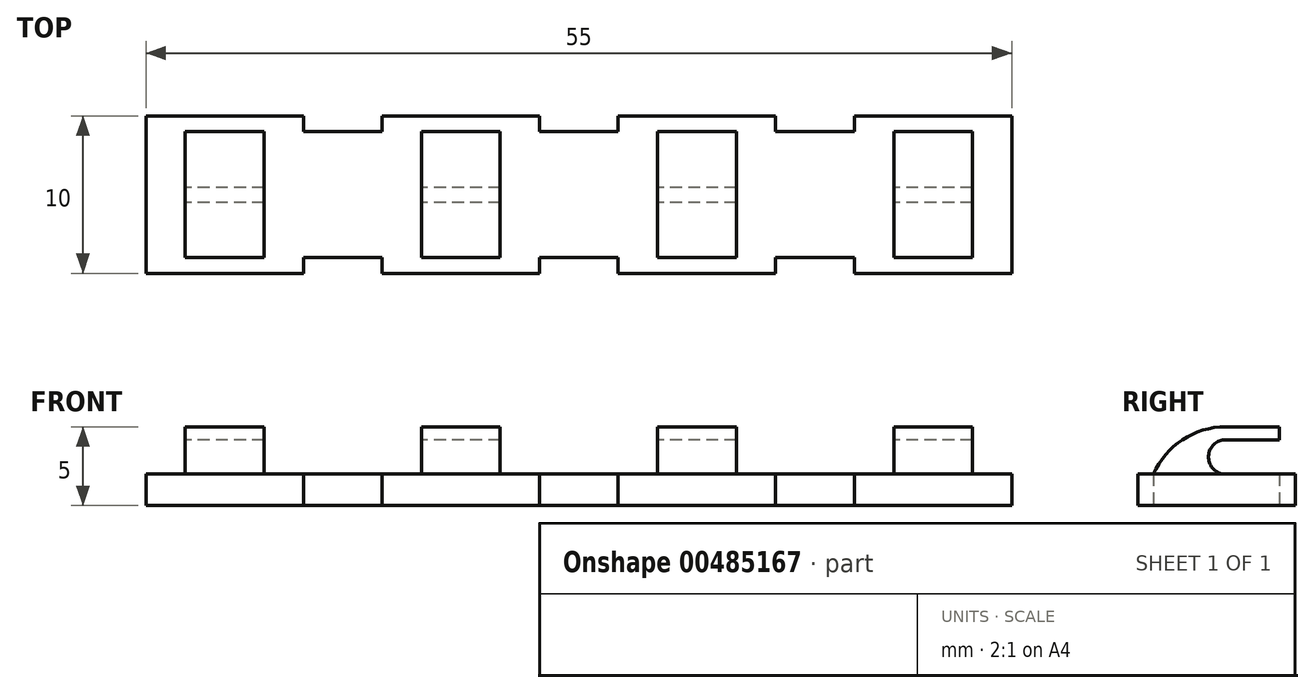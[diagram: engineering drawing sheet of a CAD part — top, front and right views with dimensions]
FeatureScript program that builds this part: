
annotation { "Feature Type Name" : "Feature", "Feature Type Description" : "" }
export const myFeature = defineFeature(function(context is Context, id is Id, definition is map)
    precondition{}
    {
        {
            var Q0;
            Q0=qCreatedBy(makeId("Top.planeOp"),FACE);
            var sketch = newSketch(context, id + "F0", { "sketchPlane" : qUnion([Q0])});
            skLineSegment(sketch, "E0.bottom", {"start": v(27.5, 5) * mm, "end": v(-27.5, 5) * mm, "construction": true});
            skLineSegment(sketch, "E0.top", {"start": v(27.5, -5) * mm, "end": v(-27.5, -5) * mm, "construction": true});
            skLineSegment(sketch, "E0.left", {"start": v(27.5, 5) * mm, "end": v(27.5, -5) * mm, "construction": true});
            skLineSegment(sketch, "E0.right", {"start": v(-27.5, 5) * mm, "end": v(-27.5, -5) * mm, "construction": true});
            skPoint(sketch, "E0.middle", {"position": v(0, 0) * mm});
            skLineSegment(sketch, "E1.bottom", {"start": v(-27.5, 5) * mm, "end": v(-17.5, 5) * mm});
            skLineSegment(sketch, "E1.top", {"start": v(-27.5, -5) * mm, "end": v(-17.5, -5) * mm});
            skLineSegment(sketch, "E1.left", {"start": v(-27.5, 5) * mm, "end": v(-27.5, -5) * mm});
            skLineSegment(sketch, "E1.right", {"start": v(-17.5, 5) * mm, "end": v(-17.5, -5) * mm});
            skLineSegment(sketch, "E2.bottom", {"start": v(-12.5, 5) * mm, "end": v(-2.5, 5) * mm});
            skLineSegment(sketch, "E2.top", {"start": v(-12.5, -5) * mm, "end": v(-2.5, -5) * mm});
            skLineSegment(sketch, "E2.left", {"start": v(-12.5, 5) * mm, "end": v(-12.5, -5) * mm});
            skLineSegment(sketch, "E2.right", {"start": v(-2.5, 5) * mm, "end": v(-2.5, -5) * mm});
            skLineSegment(sketch, "E3.bottom", {"start": v(-17.5, 4) * mm, "end": v(-12.5, 4) * mm});
            skLineSegment(sketch, "E3.top", {"start": v(-17.5, -4) * mm, "end": v(-12.5, -4) * mm});
            skLineSegment(sketch, "E3.left", {"start": v(-17.5, 4) * mm, "end": v(-17.5, -4) * mm});
            skLineSegment(sketch, "E3.right", {"start": v(-12.5, 4) * mm, "end": v(-12.5, -4) * mm});
            skLineSegment(sketch, "E4.MirrorCS", {"start": v(2.5, 5) * mm, "end": v(2.5, -5) * mm});
            skLineSegment(sketch, "E5.MirrorCS", {"start": v(12.5, 5) * mm, "end": v(2.5, 5) * mm});
            skLineSegment(sketch, "E6.MirrorCS", {"start": v(12.5, 5) * mm, "end": v(12.5, -5) * mm});
            skLineSegment(sketch, "E7.MirrorCS", {"start": v(12.5, -5) * mm, "end": v(2.5, -5) * mm});
            skLineSegment(sketch, "E8.MirrorCS", {"start": v(17.5, -4) * mm, "end": v(12.5, -4) * mm});
            skLineSegment(sketch, "E9.MirrorCS", {"start": v(17.5, 4) * mm, "end": v(12.5, 4) * mm});
            skLineSegment(sketch, "E10.MirrorCS", {"start": v(27.5, 5) * mm, "end": v(17.5, 5) * mm});
            skLineSegment(sketch, "E11.MirrorCS", {"start": v(17.5, 5) * mm, "end": v(17.5, -5) * mm});
            skLineSegment(sketch, "E12.MirrorCS", {"start": v(27.5, -5) * mm, "end": v(17.5, -5) * mm});
            skLineSegment(sketch, "E13.MirrorCS", {"start": v(27.5, 5) * mm, "end": v(27.5, -5) * mm});
            skLineSegment(sketch, "E14.bottom", {"start": v(-2.5, 4) * mm, "end": v(2.5, 4) * mm});
            skLineSegment(sketch, "E14.top", {"start": v(-2.5, -4) * mm, "end": v(2.5, -4) * mm});
            skLineSegment(sketch, "E14.left", {"start": v(-2.5, 4) * mm, "end": v(-2.5, -4) * mm});
            skLineSegment(sketch, "E14.right", {"start": v(2.5, 4) * mm, "end": v(2.5, -4) * mm});
            skLineSegment(sketch, "E15.bottom", {"start": v(-25, 4) * mm, "end": v(-20, 4) * mm});
            skLineSegment(sketch, "E15.top", {"start": v(-25, -4) * mm, "end": v(-20, -4) * mm});
            skLineSegment(sketch, "E15.left", {"start": v(-25, 4) * mm, "end": v(-25, -4) * mm});
            skLineSegment(sketch, "E15.right", {"start": v(-20, 4) * mm, "end": v(-20, -4) * mm});
            skPoint(sketch, "E16.oppositeSnap0", {"position": v(-15, -4) * mm});
            skLineSegment(sketch, "E16.bottom", {"start": v(-10, 4) * mm, "end": v(-5, 4) * mm});
            skLineSegment(sketch, "E16.top", {"start": v(-10, -4) * mm, "end": v(-5, -4) * mm});
            skLineSegment(sketch, "E16.left", {"start": v(-10, 4) * mm, "end": v(-10, -4) * mm});
            skLineSegment(sketch, "E16.right", {"start": v(-5, 4) * mm, "end": v(-5, -4) * mm});
            skLineSegment(sketch, "E17.MirrorCS", {"start": v(10, 4) * mm, "end": v(10, -4) * mm});
            skLineSegment(sketch, "E18.MirrorCS", {"start": v(10, 4) * mm, "end": v(5, 4) * mm});
            skLineSegment(sketch, "E19.MirrorCS", {"start": v(5, 4) * mm, "end": v(5, -4) * mm});
            skLineSegment(sketch, "E20.MirrorCS", {"start": v(10, -4) * mm, "end": v(5, -4) * mm});
            skLineSegment(sketch, "E21.MirrorCS", {"start": v(20, 4) * mm, "end": v(20, -4) * mm});
            skLineSegment(sketch, "E22.MirrorCS", {"start": v(25, -4) * mm, "end": v(20, -4) * mm});
            skLineSegment(sketch, "E23.MirrorCS", {"start": v(25, 4) * mm, "end": v(20, 4) * mm});
            skLineSegment(sketch, "E24.MirrorCS", {"start": v(25, 4) * mm, "end": v(25, -4) * mm});
            skSolve(sketch);
        }
        {
            var Q0;
            Q0 = qSketchRegion(id + "F0", true);
            extrude(context, id + "F1", {"entities" : qUnion([Q0]), "depth" : 2 * mm});
        }
        {
            var Q0;
            Q0=makeQuery(id+"F0.imprint","IMPRINT",FACE,{"disambiguationData":[TD([[makeQuery(id+"F0.imprint","IMPRINT",EDGE,{"derivedFrom":sQuery(id+"F0.wireOp",EDGE,"E15.bottom")}),-1.0]])]});
            var Q1;
            Q1=makeQuery(id+"F0.imprint","IMPRINT",FACE,{"disambiguationData":[TD([[makeQuery(id+"F0.imprint","IMPRINT",EDGE,{"derivedFrom":sQuery(id+"F0.wireOp",EDGE,"E16.bottom")}),-1.0]])]});
            var Q2;
            Q2=makeQuery(id+"F0.imprint","IMPRINT",FACE,{"disambiguationData":[TD([[makeQuery(id+"F0.imprint","IMPRINT",EDGE,{"derivedFrom":sQuery(id+"F0.wireOp",EDGE,"E17.MirrorCS")}),-1.0]])]});
            var Q3;
            Q3=makeQuery(id+"F0.imprint","IMPRINT",FACE,{"disambiguationData":[TD([[makeQuery(id+"F0.imprint","IMPRINT",EDGE,{"derivedFrom":sQuery(id+"F0.wireOp",EDGE,"E21.MirrorCS")}),1.0]])]});
            extrude(context, id + "F2", {"entities" : qUnion([Q0, Q1, Q2, Q3]), "operationType" : NewBodyOperationType.ADD, "depth" : 5 * mm});
        }
        {
            var Q0;
            Q0=makeQuery(id+"F2.opExtrude","CAP_EDGE",EDGE,{"disambiguationData":[OSD([sQuery(id+"F0.wireOp",EDGE,"E15.top")])],"isStart":false});
            var Q1;
            Q1=makeQuery(id+"F2.opExtrude","CAP_EDGE",EDGE,{"disambiguationData":[OSD([sQuery(id+"F0.wireOp",EDGE,"E16.top")])],"isStart":false});
            var Q2;
            Q2=makeQuery(id+"F2.opExtrude","CAP_EDGE",EDGE,{"disambiguationData":[OSD([sQuery(id+"F0.wireOp",EDGE,"E20.MirrorCS")])],"isStart":false});
            var Q3;
            Q3=makeQuery(id+"F2.opExtrude","CAP_EDGE",EDGE,{"disambiguationData":[OSD([sQuery(id+"F0.wireOp",EDGE,"E22.MirrorCS")])],"isStart":false});
            fillet(context, id + "F3", {"entities" : qUnion([Q0, Q1, Q2, Q3]), "radius" : 5 * mm, "tangentPropagation" : true, "allowEdgeOverflow" : false});
        }
        {
            var Q0;
            Q0=makeQuery(id+"F2.opExtrude","SWEPT_FACE",FACE,{"disambiguationData":[OSD([sQuery(id+"F0.wireOp",EDGE,"E15.left")])]});
            var sketch = newSketch(context, id + "F4", { "sketchPlane" : qUnion([Q0])});
            skLineSegment(sketch, "E25", {"start": v(-4, 5) * mm, "end": v(-4, 4.18) * mm});
            skLineSegment(sketch, "E26", {"start": v(-4, 4.18) * mm, "end": v(-0.58, 4.18) * mm});
            skArc(sketch, "E27", {"start": v(-0.47, 2) * mm, "mid": v(0.5, 3.15) * mm, "end": v(-0.58, 4.18) * mm});
            skSolve(sketch);
        }
        {
            var Q0;
            {var subQ0=sQuery(id+"F4.wireOp",EDGE,"E26");Q0=makeQuery(id+"F4.imprint","IMPRINT",FACE,{"disambiguationData":[TD([[makeQuery(id+"F4.imprint","IMPRINT",EDGE,{"derivedFrom":subQ0}),-1.0]])]});}
            extrude(context, id + "F5", {"entities" : qUnion([Q0]), "operationType" : NewBodyOperationType.REMOVE, "oppositeDirection" : true, "depth" : 65 * mm});
        }
    });
